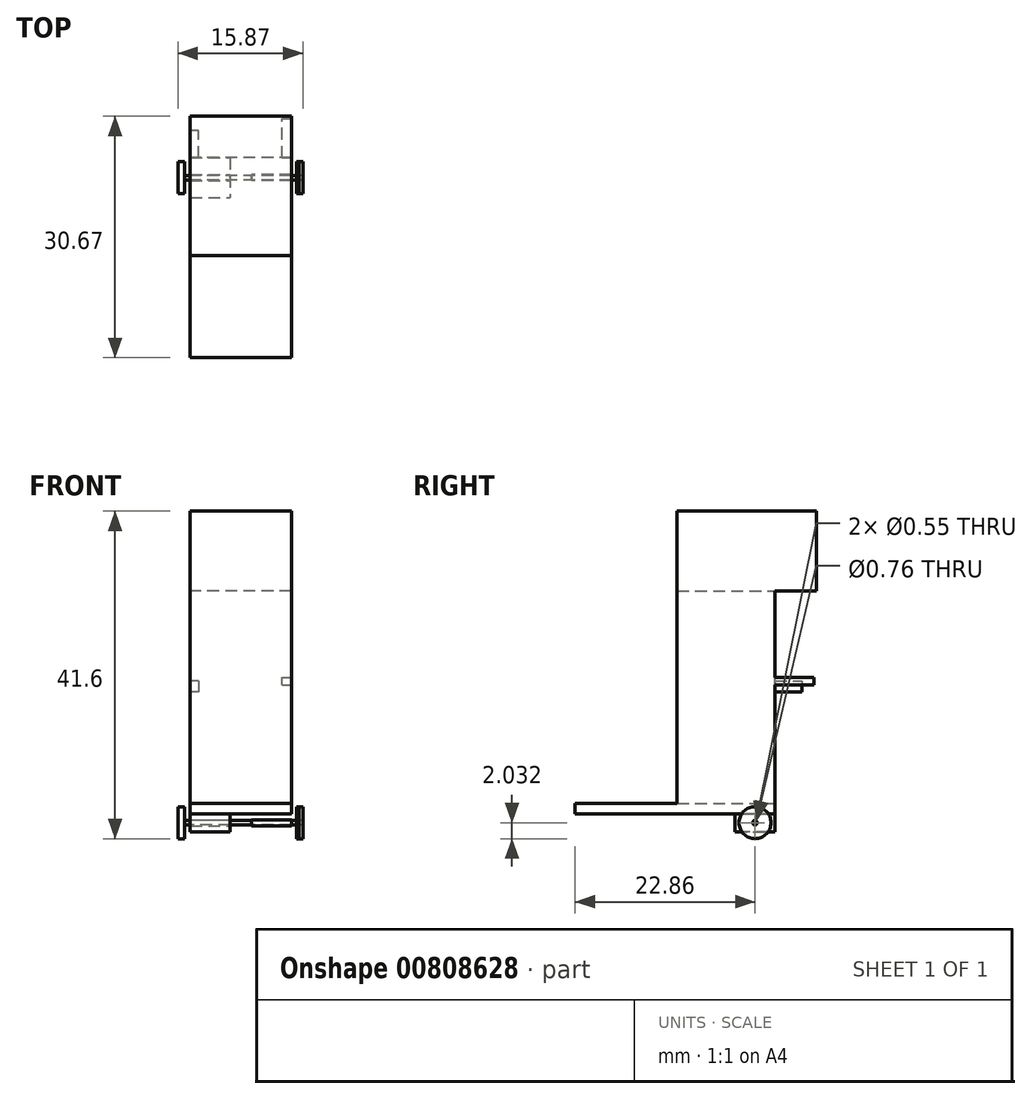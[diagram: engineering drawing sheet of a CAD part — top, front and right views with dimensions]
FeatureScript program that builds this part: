
annotation { "Feature Type Name" : "Feature", "Feature Type Description" : "" }
export const myFeature = defineFeature(function(context is Context, id is Id, definition is map)
    precondition{}
    {
        {
            var Q0;
            Q0=qCreatedBy(makeId("Front.planeOp"),FACE);
            var sketch = newSketch(context, id + "F0", { "sketchPlane" : qUnion([Q0])});
            skLineSegment(sketch, "E0.bottom", {"start": v(0, 0) * mm, "end": v(-12.89, 0) * mm});
            skLineSegment(sketch, "E0.top", {"start": v(0, 27.02) * mm, "end": v(-12.89, 27.02) * mm});
            skLineSegment(sketch, "E0.left", {"start": v(0, 0) * mm, "end": v(0, 27.02) * mm});
            skLineSegment(sketch, "E0.right", {"start": v(-12.89, 0) * mm, "end": v(-12.89, 27.02) * mm});
            skSolve(sketch);
        }
        {
            var Q0;
            Q0 = qSketchRegion(id + "F0", true);
            extrude(context, id + "F1", {"entities" : qUnion([Q0]), "depth" : 12.45 * mm, "offsetDistance" : 25.4 * mm});
        }
        {
            var Q0;
            Q0=qCreatedBy(makeId("Front.planeOp"),FACE);
            var sketch = newSketch(context, id + "F2", { "sketchPlane" : qUnion([Q0])});
            skLineSegment(sketch, "E1.bottom", {"start": v(-12.87, 0) * mm, "end": v(0, 0) * mm});
            skLineSegment(sketch, "E1.top", {"start": v(-12.87, -1.3) * mm, "end": v(0, -1.3) * mm});
            skLineSegment(sketch, "E1.left", {"start": v(-12.87, 0) * mm, "end": v(-12.87, -1.3) * mm});
            skLineSegment(sketch, "E1.right", {"start": v(0, 0) * mm, "end": v(0, -1.3) * mm});
            skSolve(sketch);
        }
        {
            var Q0;
            Q0=makeQuery(id+"F2.imprint","IMPRINT",FACE,{"disambiguationData":[TD([[makeQuery(id+"F2.imprint","IMPRINT",EDGE,{"derivedFrom":sQuery(id+"F2.wireOp",EDGE,"E1.bottom")}),-1.0]])]});
            extrude(context, id + "F3", {"entities" : qUnion([Q0]), "operationType" : NewBodyOperationType.ADD, "depth" : 25.4 * mm, "offsetDistance" : 25.4 * mm});
        }
        {
            var Q0;
            Q0=makeQuery(id+"F3.opExtrude","SWEPT_FACE",FACE,{"disambiguationData":[OSD([sQuery(id+"F2.wireOp",EDGE,"E1.top")])]});
            var sketch = newSketch(context, id + "F4", { "sketchPlane" : qUnion([Q0])});
            skLineSegment(sketch, "E2.bottom", {"start": v(0, 0) * mm, "end": v(-5.08, 0) * mm});
            skLineSegment(sketch, "E2.top", {"start": v(0, 5.08) * mm, "end": v(-5.08, 5.08) * mm});
            skLineSegment(sketch, "E2.left", {"start": v(0, 0) * mm, "end": v(0, 5.08) * mm});
            skLineSegment(sketch, "E2.right", {"start": v(-5.08, 0) * mm, "end": v(-5.08, 5.08) * mm});
            skLineSegment(sketch, "E3", {"start": v(-6.43, 0) * mm, "end": v(-6.43, 1.13) * mm});
            skLineSegment(sketch, "E4.MirrorCS", {"start": v(-7.79, 0) * mm, "end": v(-7.79, 5.08) * mm});
            skLineSegment(sketch, "E5.MirrorCS", {"start": v(-12.87, 5.08) * mm, "end": v(-7.79, 5.08) * mm});
            skLineSegment(sketch, "E6.MirrorCS", {"start": v(-12.87, 0) * mm, "end": v(-12.87, 5.08) * mm});
            skLineSegment(sketch, "E7.MirrorCS", {"start": v(-12.87, 0) * mm, "end": v(-7.79, 0) * mm});
            skSolve(sketch);
        }
        {
            var Q0;
            Q0 = qSketchRegion(id + "F4", true);
            extrude(context, id + "F5", {"entities" : qUnion([Q0]), "operationType" : NewBodyOperationType.ADD, "depth" : 2.3 * mm, "offsetDistance" : 25.4 * mm});
        }
        {
            var Q0;
            Q0=makeQuery(id+"F5.opExtrude","SWEPT_FACE",FACE,{"disambiguationData":[OSD([sQuery(id+"F4.wireOp",EDGE,"E2.right")])]});
            var sketch = newSketch(context, id + "F6", { "sketchPlane" : qUnion([Q0])});
            skLineSegment(sketch, "E8", {"start": v(5.08, -2.44) * mm, "end": v(0, -2.44) * mm});
            skCircle(sketch, "E9", {"center": v(2.54, -2.44) * mm, "radius": 0.38 * mm});
            skSolve(sketch);
        }
        {
            var Q0;
            {var subQ0=sQuery(id+"F6.wireOp",EDGE,"E9");var subQ1=sQuery(id+"F6.wireOp",EDGE,"E8");var subQ2=makeQuery(id+"F6.imprint","INTERSECT",VERTEX,{"disambiguationData":[OD(0.0)],"derivedFrom":[subQ1,subQ0]});Q0=makeQuery(id+"F6.imprint","IMPRINT",FACE,{"disambiguationData":[TD([[makeQuery(id+"F6.imprint","IMPRINT",EDGE,{"disambiguationData":[TD([[subQ2,-1.0]])],"derivedFrom":subQ1}),-1.0]])]});}
            var Q1;
            {var subQ0=sQuery(id+"F6.wireOp",EDGE,"E9");var subQ1=sQuery(id+"F6.wireOp",EDGE,"E8");var subQ2=makeQuery(id+"F6.imprint","INTERSECT",VERTEX,{"disambiguationData":[OD(0.0)],"derivedFrom":[subQ1,subQ0]});Q1=makeQuery(id+"F6.imprint","IMPRINT",FACE,{"disambiguationData":[TD([[makeQuery(id+"F6.imprint","IMPRINT",EDGE,{"disambiguationData":[TD([[subQ2,-1.0]])],"derivedFrom":subQ1}),1.0]])]});}
            extrude(context, id + "F7", {"entities" : qUnion([Q0, Q1]), "operationType" : NewBodyOperationType.REMOVE, "oppositeDirection" : true, "depth" : 25.4 * mm, "offsetDistance" : 25.4 * mm});
        }
        {
            var Q0;
            Q0 = qSketchRegion(id + "F6", true);
            extrude(context, id + "F8", {"entities" : qUnion([Q0]), "operationType" : NewBodyOperationType.REMOVE, "depth" : 16.13 * mm, "offsetDistance" : 25.4 * mm});
        }
        {
            var Q0;
            Q0=makeQuery(id+"F5.boolean.opBoolean","MERGE",FACE,{"derivedFrom":[makeQuery(id+"F3.opExtrude","SWEPT_FACE",FACE,{"disambiguationData":[OSD([sQuery(id+"F2.wireOp",EDGE,"E1.left")])]}),makeQuery(id+"F5.opExtrude","SWEPT_FACE",FACE,{"disambiguationData":[OSD([sQuery(id+"F4.wireOp",EDGE,"E6.MirrorCS")])]})]});
            var sketch = newSketch(context, id + "F9", { "sketchPlane" : qUnion([Q0])});
            skCircle(sketch, "E10", {"center": v(2.54, -2.44) * mm, "radius": 0.27 * mm});
            skSolve(sketch);
        }
        {
            var Q0;
            Q0=makeQuery(id+"F9.imprint","IMPRINT",FACE,{"disambiguationData":[TD([[makeQuery(id+"F9.imprint","IMPRINT",EDGE,{"derivedFrom":sQuery(id+"F9.wireOp",EDGE,"E10")}),1.0]])]});
            extrude(context, id + "F10", {"entities" : qUnion([Q0]), "oppositeDirection" : true, "depth" : 13.82 * mm, "offsetDistance" : 25.4 * mm});
        }
        {
            var Q0;
            Q0=makeQuery(id+"F9.imprint","IMPRINT",FACE,{"disambiguationData":[TD([[makeQuery(id+"F9.imprint","IMPRINT",EDGE,{"derivedFrom":sQuery(id+"F9.wireOp",EDGE,"E10")}),1.0]])]});
            extrude(context, id + "F11", {"entities" : qUnion([Q0]), "operationType" : NewBodyOperationType.ADD, "depth" : 1.04 * mm, "offsetDistance" : 25.4 * mm});
        }
        {
            var Q0;
            Q0=makeQuery(id+"F10.opExtrude","CAP_FACE",FACE,{"disambiguationData":[OSD([sQuery(id+"F9.wireOp",EDGE,"E10")])],"isStart":false});
            var sketch = newSketch(context, id + "F12", { "sketchPlane" : qUnion([Q0])});
            skCircle(sketch, "E11", {"center": v(-2.54, -2.44) * mm, "radius": 2.03 * mm});
            skSolve(sketch);
        }
        {
            var Q0;
            Q0=makeQuery(id+"F12.imprint","IMPRINT",FACE,{"disambiguationData":[TD([[makeQuery(id+"F12.imprint","IMPRINT",EDGE,{"derivedFrom":sQuery(id+"F12.wireOp",EDGE,"E11")}),1.0]])]});
            extrude(context, id + "F13", {"entities" : qUnion([Q0]), "depth" : 0.5 * mm, "offsetDistance" : 25.4 * mm});
        }
        {
            var Q0;
            Q0=makeQuery(id+"F13.opExtrude","CAP_FACE",FACE,{"disambiguationData":[OSD([sQuery(id+"F9.wireOp",EDGE,"E10"),sQuery(id+"F12.wireOp",EDGE,"E11")])],"isStart":true});
            extrude(context, id + "F14", {"entities" : qUnion([Q0]), "depth" : 0.3 * mm, "offsetDistance" : 25.4 * mm});
        }
        {
            var Q0;
            Q0=makeQuery(id+"F1.opExtrude","SWEPT_FACE",FACE,{"disambiguationData":[OSD([sQuery(id+"F0.wireOp",EDGE,"E0.right")])]});
            var sketch = newSketch(context, id + "F15", { "sketchPlane" : qUnion([Q0])});
            skLineSegment(sketch, "E12.bottom", {"start": v(1.35, 15.6) * mm, "end": v(-3.42, 15.6) * mm});
            skLineSegment(sketch, "E12.top", {"start": v(1.35, 14.17) * mm, "end": v(-3.42, 14.17) * mm});
            skLineSegment(sketch, "E12.left", {"start": v(1.35, 15.6) * mm, "end": v(1.35, 14.17) * mm});
            skLineSegment(sketch, "E12.right", {"start": v(-3.42, 15.6) * mm, "end": v(-3.42, 14.17) * mm});
            skSolve(sketch);
        }
        {
            var Q0;
            {var subQ0=sQuery(id+"F15.wireOp",EDGE,"E12.right");Q0=makeQuery(id+"F15.imprint","IMPRINT",FACE,{"disambiguationData":[TD([[makeQuery(id+"F15.imprint","IMPRINT",EDGE,{"derivedFrom":subQ0}),1.0]])]});}
            var Q1;
            {var subQ0=sQuery(id+"F15.wireOp",EDGE,"E12.left");Q1=makeQuery(id+"F15.imprint","IMPRINT",FACE,{"disambiguationData":[TD([[makeQuery(id+"F15.imprint","IMPRINT",EDGE,{"derivedFrom":subQ0}),-1.0]])]});}
            extrude(context, id + "F16", {"entities" : qUnion([Q0, Q1]), "operationType" : NewBodyOperationType.ADD, "oppositeDirection" : true, "depth" : 1.07 * mm, "offsetDistance" : 25.4 * mm});
        }
        {
            var Q0;
            Q0=makeQuery(id+"F5.boolean.opBoolean","MERGE",FACE,{"derivedFrom":[makeQuery(id+"F3.boolean.opBoolean","MERGE",FACE,{"derivedFrom":[makeQuery(id+"F1.opExtrude","SWEPT_FACE",FACE,{"disambiguationData":[OSD([sQuery(id+"F0.wireOp",EDGE,"E0.left")])]}),makeQuery(id+"F3.opExtrude","SWEPT_FACE",FACE,{"disambiguationData":[OSD([sQuery(id+"F2.wireOp",EDGE,"E1.right")])]})]}),makeQuery(id+"F5.opExtrude","SWEPT_FACE",FACE,{"disambiguationData":[OSD([sQuery(id+"F4.wireOp",EDGE,"E2.left")])]})]});
            var sketch = newSketch(context, id + "F17", { "sketchPlane" : qUnion([Q0])});
            skLineSegment(sketch, "E13.bottom", {"start": v(-1.77, 15.04) * mm, "end": v(4.95, 15.04) * mm});
            skLineSegment(sketch, "E13.top", {"start": v(-1.77, 16) * mm, "end": v(4.95, 16) * mm});
            skLineSegment(sketch, "E13.left", {"start": v(-1.77, 15.04) * mm, "end": v(-1.77, 16) * mm});
            skLineSegment(sketch, "E13.right", {"start": v(4.95, 15.04) * mm, "end": v(4.95, 16) * mm});
            skSolve(sketch);
        }
        {
            var Q0;
            {var subQ0=sQuery(id+"F17.wireOp",EDGE,"E13.right");Q0=makeQuery(id+"F17.imprint","IMPRINT",FACE,{"disambiguationData":[TD([[makeQuery(id+"F17.imprint","IMPRINT",EDGE,{"derivedFrom":subQ0}),1.0]])]});}
            var Q1;
            {var subQ0=sQuery(id+"F17.wireOp",EDGE,"E13.left");Q1=makeQuery(id+"F17.imprint","IMPRINT",FACE,{"disambiguationData":[TD([[makeQuery(id+"F17.imprint","IMPRINT",EDGE,{"derivedFrom":subQ0}),-1.0]])]});}
            extrude(context, id + "F18", {"entities" : qUnion([Q0, Q1]), "operationType" : NewBodyOperationType.ADD, "oppositeDirection" : true, "depth" : 1.17 * mm, "offsetDistance" : 25.4 * mm});
        }
        {
            var Q0;
            Q0=makeQuery(id+"F1.opExtrude","SWEPT_FACE",FACE,{"disambiguationData":[OSD([sQuery(id+"F0.wireOp",EDGE,"E0.top")])]});
            var sketch = newSketch(context, id + "F19", { "sketchPlane" : qUnion([Q0])});
            skLineSegment(sketch, "E14.bottom", {"start": v(0, -12.45) * mm, "end": v(-12.87, -12.45) * mm});
            skLineSegment(sketch, "E14.top", {"start": v(0, 5.27) * mm, "end": v(-12.87, 5.27) * mm});
            skLineSegment(sketch, "E14.left", {"start": v(0, -12.45) * mm, "end": v(0, 5.27) * mm});
            skLineSegment(sketch, "E14.right", {"start": v(-12.87, -12.45) * mm, "end": v(-12.87, 5.27) * mm});
            skSolve(sketch);
        }
        {
            var Q0;
            {var subQ0=sQuery(id+"F19.wireOp",EDGE,"E14.top");Q0=makeQuery(id+"F19.imprint","IMPRINT",FACE,{"disambiguationData":[TD([[makeQuery(id+"F19.imprint","IMPRINT",EDGE,{"derivedFrom":subQ0}),1.0]])]});}
            var Q1;
            {var subQ0=sQuery(id+"F19.wireOp",EDGE,"E14.bottom");Q1=makeQuery(id+"F19.imprint","IMPRINT",FACE,{"disambiguationData":[TD([[makeQuery(id+"F19.imprint","IMPRINT",EDGE,{"derivedFrom":subQ0}),-1.0]])]});}
            extrude(context, id + "F20", {"entities" : qUnion([Q0, Q1]), "operationType" : NewBodyOperationType.ADD, "depth" : 10.1 * mm, "offsetDistance" : 25.4 * mm});
        }
        {
            var Q0;
            Q0=makeQuery(id+"F11.opExtrude","CAP_FACE",FACE,{"disambiguationData":[OSD([sQuery(id+"F9.wireOp",EDGE,"E10")])],"isStart":false});
            var sketch = newSketch(context, id + "F21", { "sketchPlane" : qUnion([Q0])});
            skCircle(sketch, "E15", {"center": v(2.54, -2.44) * mm, "radius": 2.03 * mm});
            skSolve(sketch);
        }
        {
            var Q0;
            Q0 = qSketchRegion(id + "F21", true);
            extrude(context, id + "F22", {"entities" : qUnion([Q0]), "operationType" : NewBodyOperationType.ADD, "depth" : 0.5 * mm, "offsetDistance" : 25.4 * mm});
        }
        {
            var Q0;
            Q0=makeQuery(id+"F22.boolean.opBoolean","MERGE",FACE,{"derivedFrom":[makeQuery(id+"F11.opExtrude","CAP_FACE",FACE,{"disambiguationData":[OSD([sQuery(id+"F9.wireOp",EDGE,"E10")])],"isStart":false}),makeQuery(id+"F22.opExtrude","CAP_FACE",FACE,{"disambiguationData":[OSD([sQuery(id+"F21.wireOp",EDGE,"E15")])],"isStart":true})]});
            extrude(context, id + "F23", {"entities" : qUnion([Q0]), "operationType" : NewBodyOperationType.ADD, "depth" : 0.3 * mm, "offsetDistance" : 25.4 * mm});
        }
    });
